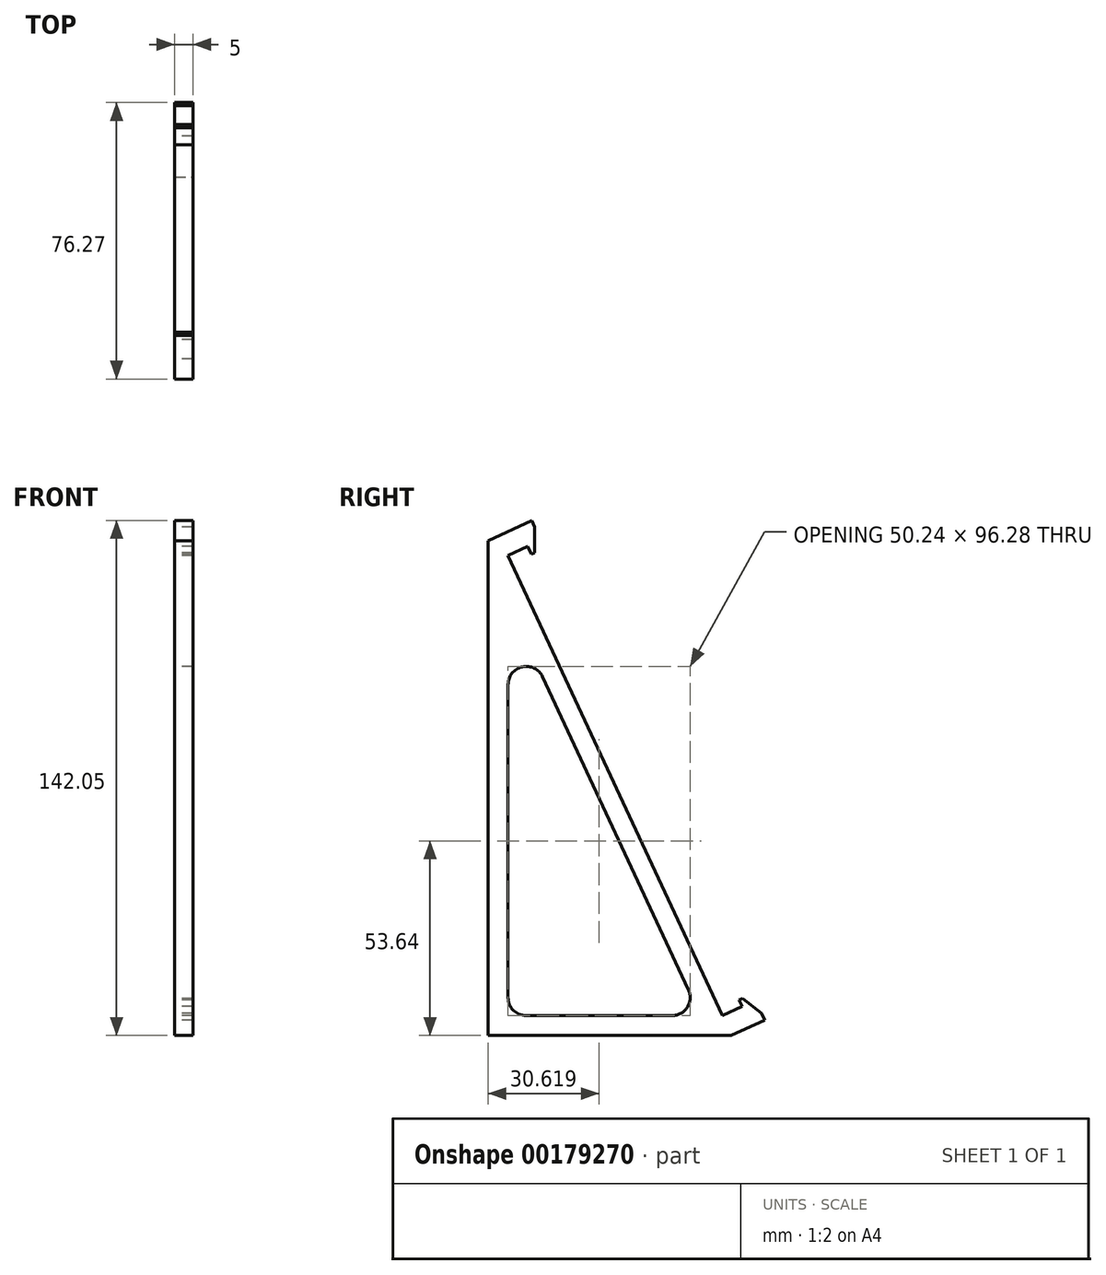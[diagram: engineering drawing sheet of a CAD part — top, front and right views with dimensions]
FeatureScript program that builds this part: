
annotation { "Feature Type Name" : "Feature", "Feature Type Description" : "" }
export const myFeature = defineFeature(function(context is Context, id is Id, definition is map)
    precondition{}
    {
        {
            var Q0;
            Q0=qCreatedBy(makeId("Right.planeOp"),FACE);
            var sketch = newSketch(context, id + "F0", { "sketchPlane" : qUnion([Q0])});
            skLineSegment(sketch, "E0", {"start": v(0, 0) * mm, "end": v(0, 126.88) * mm, "construction": true});
            skLineSegment(sketch, "E1", {"start": v(0, 0) * mm, "end": v(96.83, 0) * mm, "construction": true});
            skLineSegment(sketch, "E2", {"start": v(0, 126.88) * mm, "end": v(59.17, 0) * mm});
            skLineSegment(sketch, "E3", {"start": v(0, 126.88) * mm, "end": v(5.44, 129.42) * mm});
            skLineSegment(sketch, "E4", {"start": v(5.44, 129.42) * mm, "end": v(6.47, 127.21) * mm});
            skLineSegment(sketch, "E5", {"start": v(6.47, 127.21) * mm, "end": v(7.37, 127.64) * mm});
            skLineSegment(sketch, "E6", {"start": v(7.37, 127.64) * mm, "end": v(7.37, 134.73) * mm});
            skLineSegment(sketch, "E7", {"start": v(7.37, 134.73) * mm, "end": v(6.53, 136.55) * mm});
            skLineSegment(sketch, "E8", {"start": v(6.53, 136.55) * mm, "end": v(-5.5, 130.94) * mm});
            skLineSegment(sketch, "E9", {"start": v(-5.5, 130.94) * mm, "end": v(-5.5, -5.5) * mm});
            skLineSegment(sketch, "E10", {"start": v(-5.5, -5.5) * mm, "end": v(61.57, -5.5) * mm});
            skLineSegment(sketch, "E11", {"start": v(61.57, -5.5) * mm, "end": v(70.77, -1.21) * mm});
            skLineSegment(sketch, "E12", {"start": v(70.77, -1.21) * mm, "end": v(69.92, 0.6) * mm});
            skLineSegment(sketch, "E13", {"start": v(69.92, 0.6) * mm, "end": v(64.67, 4.77) * mm});
            skLineSegment(sketch, "E14", {"start": v(64.67, 4.77) * mm, "end": v(63.76, 4.35) * mm});
            skLineSegment(sketch, "E15", {"start": v(63.76, 4.35) * mm, "end": v(64.6, 2.54) * mm});
            skLineSegment(sketch, "E16", {"start": v(64.6, 2.54) * mm, "end": v(59.17, 0) * mm});
            skLineSegment(sketch, "E17", {"start": v(0, 113.87) * mm, "end": v(53.1, 0) * mm});
            skLineSegment(sketch, "E18", {"start": v(0, 113.87) * mm, "end": v(0, 0) * mm});
            skLineSegment(sketch, "E19", {"start": v(53.1, 0) * mm, "end": v(0, 0) * mm});
            skSolve(sketch);
        }
        {
            var Q0;
            Q0=makeQuery(id+"F0.imprint","IMPRINT",FACE,{"disambiguationData":[TD([[makeQuery(id+"F0.imprint","IMPRINT",EDGE,{"derivedFrom":sQuery(id+"F0.wireOp",EDGE,"E2")}),-1.0]])]});
            extrude(context, id + "F1", {"entities" : qUnion([Q0]), "depth" : 5 * mm});
        }
        {
            var Q0;
            Q0=makeQuery(id+"F1.opExtrude","SWEPT_EDGE",EDGE,{"disambiguationData":[OSD([sQuery(id+"F0.wireOp",EDGE,"E17"),sQuery(id+"F0.wireOp",EDGE,"E18")])]});
            var Q1;
            Q1=makeQuery(id+"F1.opExtrude","SWEPT_EDGE",EDGE,{"disambiguationData":[OSD([sQuery(id+"F0.wireOp",EDGE,"E17"),sQuery(id+"F0.wireOp",EDGE,"E19")])]});
            var Q2;
            Q2=makeQuery(id+"F1.opExtrude","SWEPT_EDGE",EDGE,{"disambiguationData":[OSD([sQuery(id+"F0.wireOp",EDGE,"E18"),sQuery(id+"F0.wireOp",EDGE,"E19")])]});
            fillet(context, id + "F2", {"entities" : qUnion([Q0, Q1, Q2]), "radius" : 5 * mm, "tangentPropagation" : true, "allowEdgeOverflow" : false});
        }
    });
